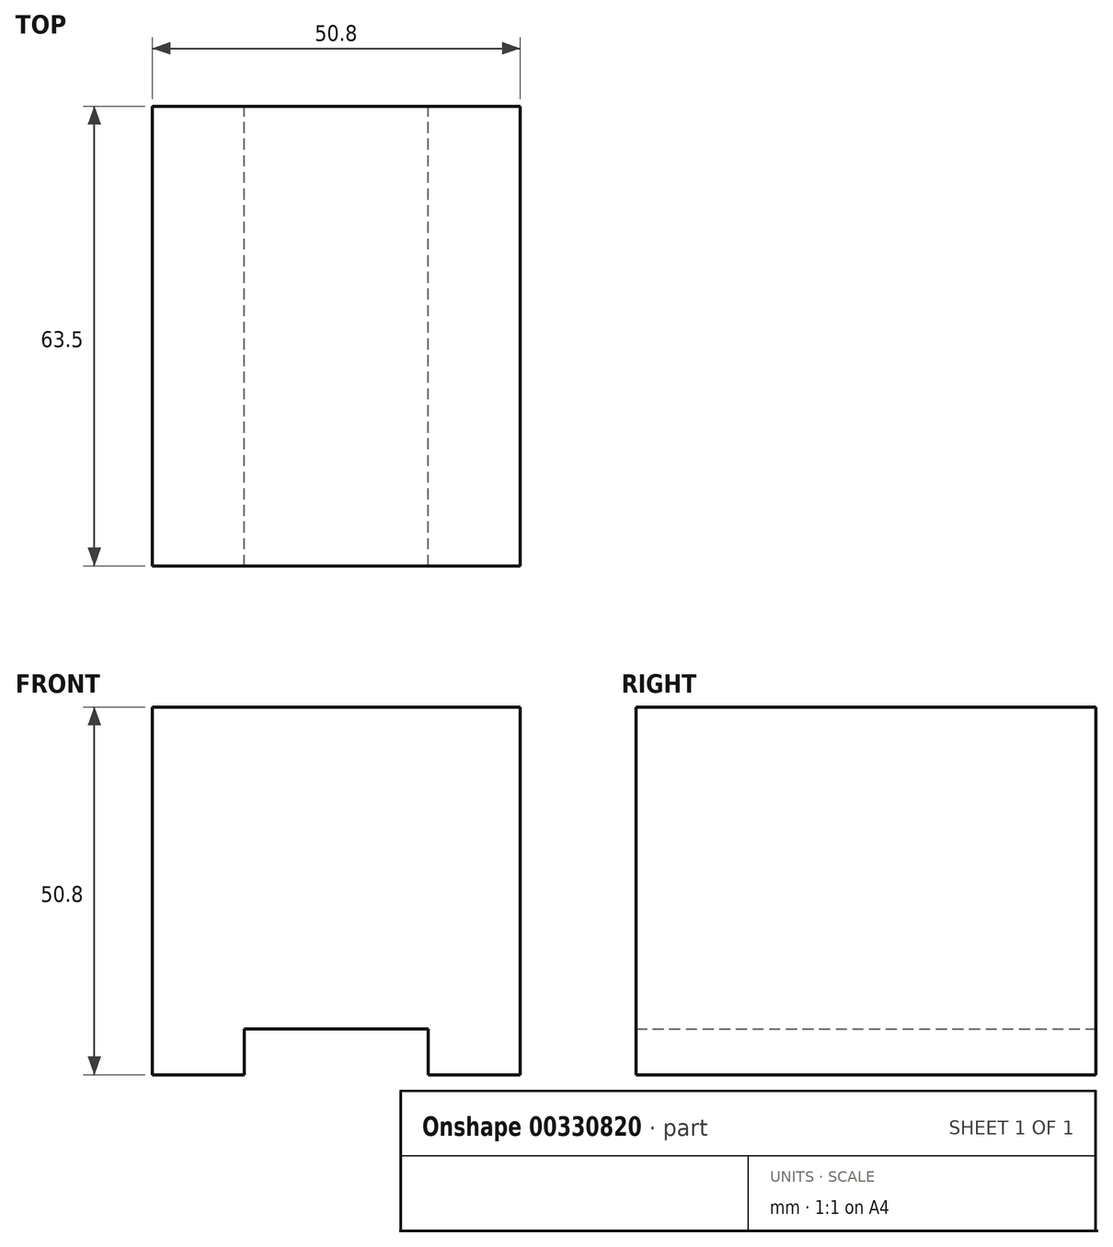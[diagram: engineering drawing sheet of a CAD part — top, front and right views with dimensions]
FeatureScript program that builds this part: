
annotation { "Feature Type Name" : "Feature", "Feature Type Description" : "" }
export const myFeature = defineFeature(function(context is Context, id is Id, definition is map)
    precondition{}
    {
        {
            var Q0;
            Q0=qCreatedBy(makeId("Front.planeOp"),FACE);
            var sketch = newSketch(context, id + "F0", { "sketchPlane" : qUnion([Q0])});
            skLineSegment(sketch, "E0.bottom", {"start": v(-25.4, -25.4) * mm, "end": v(-12.7, -25.4) * mm});
            skLineSegment(sketch, "E0.top", {"start": v(-25.4, 25.4) * mm, "end": v(25.4, 25.4) * mm});
            skLineSegment(sketch, "E0.left", {"start": v(-25.4, -25.4) * mm, "end": v(-25.4, 25.4) * mm});
            skLineSegment(sketch, "E0.right", {"start": v(25.4, -25.4) * mm, "end": v(25.4, 25.4) * mm});
            skPoint(sketch, "E0.middle", {"position": v(0, 0) * mm});
            skLineSegment(sketch, "E1.0", {"start": v(-12.7, -25.4) * mm, "end": v(-12.7, -19.05) * mm});
            skLineSegment(sketch, "E2.0", {"start": v(12.7, -25.4) * mm, "end": v(12.7, -19.05) * mm});
            skLineSegment(sketch, "E3.0", {"start": v(-12.7, -19.05) * mm, "end": v(12.7, -19.05) * mm});
            skLineSegment(sketch, "E4.trimOffspring", {"start": v(12.7, -25.4) * mm, "end": v(25.4, -25.4) * mm});
            skSolve(sketch);
        }
        {
            var Q0;
            Q0=makeQuery(id+"F0.imprint","IMPRINT",FACE,{"disambiguationData":[TD([[makeQuery(id+"F0.imprint","IMPRINT",EDGE,{"derivedFrom":sQuery(id+"F0.wireOp",EDGE,"E0.bottom")}),1.0]])]});
            extrude(context, id + "F1", {"entities" : qUnion([Q0]), "depth" : 63.5 * mm});
        }
    });
